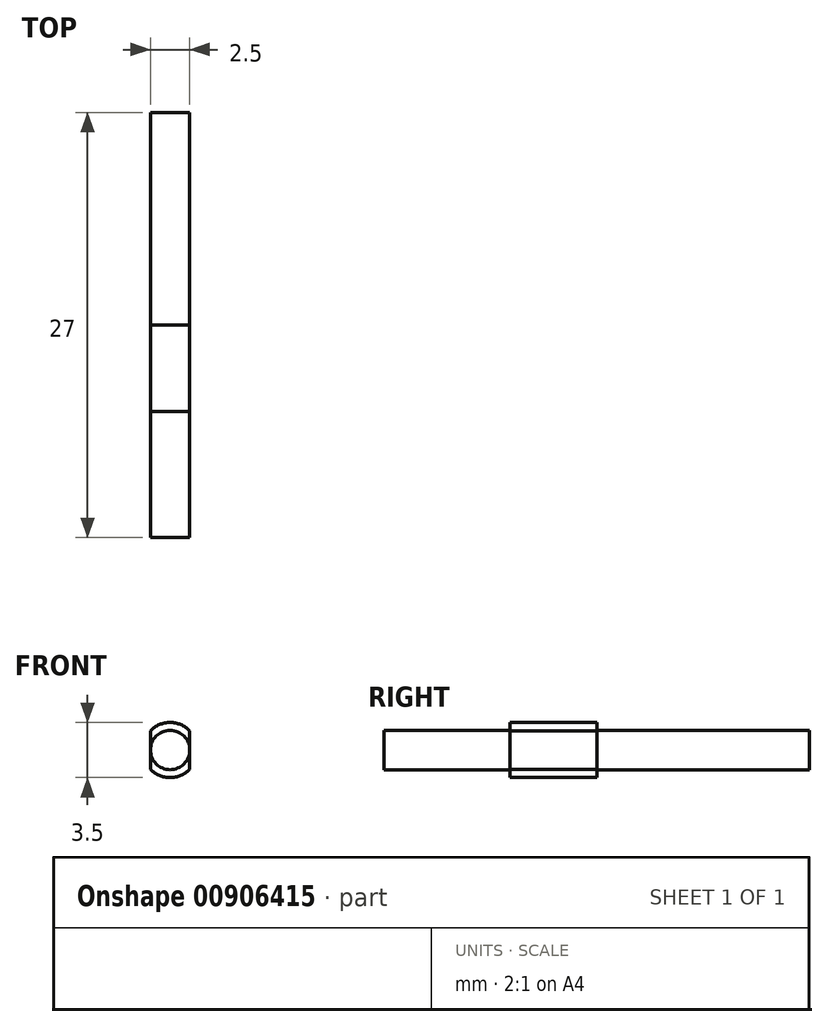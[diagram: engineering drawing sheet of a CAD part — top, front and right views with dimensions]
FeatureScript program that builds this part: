
annotation { "Feature Type Name" : "Feature", "Feature Type Description" : "" }
export const myFeature = defineFeature(function(context is Context, id is Id, definition is map)
    precondition{}
    {
        {
            var Q0;
            Q0=qCreatedBy(makeId("Front.planeOp"),FACE);
            var sketch = newSketch(context, id + "F0", { "sketchPlane" : qUnion([Q0])});
            skArc(sketch, "E0", {"start": v(-1.25, -1.22) * mm, "mid": v(0, -1.75) * mm, "end": v(1.25, -1.22) * mm});
            skLineSegment(sketch, "E1", {"start": v(-1.25, 1.22) * mm, "end": v(-1.25, -1.22) * mm});
            skLineSegment(sketch, "E2", {"start": v(1.25, 1.22) * mm, "end": v(1.25, -1.22) * mm});
            skArc(sketch, "E3.trimOffspring", {"start": v(1.25, 1.22) * mm, "mid": v(0, 1.75) * mm, "end": v(-1.25, 1.22) * mm});
            skSolve(sketch);
        }
        {
            var Q0;
            Q0=qSketchRegion(id+"F0",true);
            extrude(context, id + "F1", {"entities" : qUnion([Q0]), "depth" : 5.5 * mm, "offsetDistance" : 25 * mm});
        }
        {
            var Q0;
            Q0=qCreatedBy(makeId("Front.planeOp"),FACE);
            var sketch = newSketch(context, id + "F2", { "sketchPlane" : qUnion([Q0])});
            skCircle(sketch, "E4", {"center": v(0, 0) * mm, "radius": 1.25 * mm});
            skSolve(sketch);
        }
        {
            var Q0;
            Q0=qSketchRegion(id+"F2",true);
            extrude(context, id + "F3", {"entities" : qUnion([Q0]), "operationType" : NewBodyOperationType.ADD, "endBound" : BoundingType.SYMMETRIC, "depth" : 27 * mm, "offsetDistance" : 25 * mm});
        }
    });
